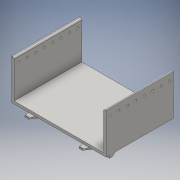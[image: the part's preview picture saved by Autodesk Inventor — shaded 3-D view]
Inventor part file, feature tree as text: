
AUTODESK INVENTOR PART (.ipt)
format: ipt  version: 2016 (Build 200138000, 138)  size: 183,808 bytes
history: native  units: in
note: dims shown in document units (in); Inventor stores cm internally (conversion verified against a paired STEP export)
features: sketch x5, extrude x3, other x1, hole x1, pattern_linear x1
ambient origin geometry x8: Origin, YZ Plane, XZ Plane, XY Plane, X Axis, Y Axis, Z Axis, Center Point
bodies: Solid1 (feature_tree)
feature tree (11):
  extrude  "Extrusion1"  Depth=0.125in
  sketch  "Sketch18"  dims[d6=0.075in d7=0.2in]
  extrude  "Extrusion3"  Depth=0.2in
  other  "Snap Fit1"
  sketch  "Sketch20"  dims[d176=3.0in]
  hole  "Hole8"  [1 undecoded]
  pattern_linear  "Rectangular Pattern4"  Spacing1=1.5in  [1 undecoded]
  extrude  "Extrusion4"  Depth=7.0in
  sketch  "Sketch1"  dims[d0=7.0in d4=0.125in]
  sketch  "Sketch19"  dims[d9=0.125in d32=5.0in d33=0.0in]
  sketch  "Sketch21"  dims[d177=3.0in d180=1.5in d184=7.0in d187=7.0in d188=0.0in d189=0.3in d190=0.08in d191=0.14in d192=0.08in d193=0.5in d194=0.3in d195=0.03in d196=0.05in d197=0.3436in d198=0.3436in d199=2.5in d232=1.0in d233=1.0in d215=0.1575in d216=0.75in d217=0.375in d218=0.25in d219=0.5635in d220=1.0in d221=0.8108in d227=3.1496in d229=0.625in d243=0.2in d245=0.25in d246=7.0in d247=0.0in d248=1.5in d34=1.0in d35=1.0in d80=1.0in d81=1.0in d119=1.0in d120=1.0in]
note: 2 required parameter values undecoded (feature->parameter linkage not recoverable at this tier; creation-order binding heuristic only, values carry confidence <= 0.55)
